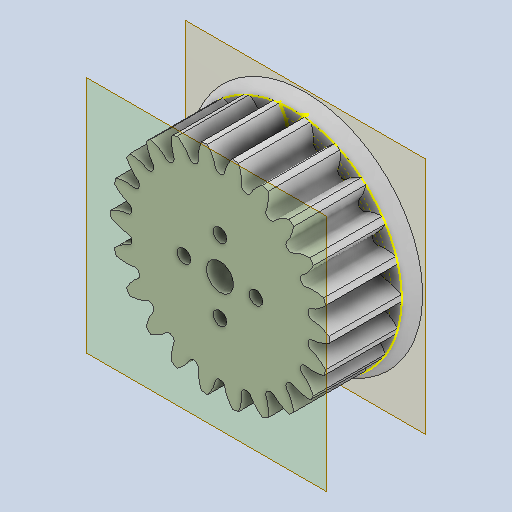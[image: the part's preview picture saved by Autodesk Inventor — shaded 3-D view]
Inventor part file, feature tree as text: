
AUTODESK INVENTOR PART (.ipt)
format: ipt  version: 2024.2 (Build 282272000, 272)  size: 420,352 bytes
history: native  units: mm
features: other x6, sketch x6
ambient origin geometry x8: Origin, YZ Plane, XZ Plane, XY Plane, X Axis, Y Axis, Z Axis, Center Point
bodies: Body1 (feature_tree)
feature tree (12):
  other  "Шест.ipt"
  other  "Твердое тело1::Шест.ipt"
  other  "Элемент создания тегов1"
  sketch  "Sketch1"  dims[d0=10.0mm]
  sketch  "Эскиз2"
  sketch  "Эскиз3"
  sketch  "Эскиз4"
  sketch  "Эскиз5"
  sketch  "Эскиз6"
  other  "РабПлоскость1"
  other  "РабПлоскость2"
  other  "Твердое тело1"
